# Revit family: Lighting_Pendants_Nordlux_Angle_E27
name_source: partatom
category: Lighting Fixtures
revit_build: Autodesk Revit 2017 (Build: 20190508_0315(x64)
units: mm (PartAtom-declared; Revit-internal decimal feet)

## family parameters
Always vertical = Yes
Cut with Voids When Loaded = No
Light Source = Yes
OmniClass Number = 23.80.70.00
OmniClass Title = Lighting
Part Type = Normal
Room Calculation Point = No
Round Connector Dimension = Use Diameter
Shared = No
Work Plane-Based = No

## types (3) — shared parameters
AssetType = Fixed
BIMObjectName = Lighting_Pendants_Nordlux_Angle_E27
Brand = Nordlux
Category = Pendants
Collection = Angle E27
Color Filter = 16777215
ConvergoRefNr = 0143-2009-0015-DK
DefaultElevation = 4000 mm  [stored 13.1234 ft]
Designer = Maria Berntsen
Dimming Lamp Color Temperature Shift = <None>
DurationUnit = Hours
Features = Lamp can be dimmed with compatible bulb.Magnet on the textile cord for directing the light in any direction.
HasProtectiveEarth = No
IP_Code = IP20
IfcExportAs = IfcLightFixtureType
IfcExportType = NOTDEFINED
InsulationStandardClass = Class 2 Double Isolated
Light Source Symbol Length = 300 mm
LightFixtureMountingType = Suspended
LightFixturePlacingType = Ceiling
Manufacturer = Nordlux
ManufacturerName = Nordlux
ManufacturerURL = https://www.nordlux.com
Material = Metal & Plastic
NBSDescription = General purpose luminaires
NBSReference = 90-60-50/405
Name = Angle_E27
NominalCurrent = 0 A
NominalDiameter = 206 mm
NominalFrequencyRange = 50 Hz
NominalHeight = 247 mm
NominalLength = 206 mm
NominalRadius = 103 mm
NominalVoltage = 230 V
NominalVoltageCalc = 0 V
NominalWidth = 206 mm
NumberOfPoles = 1
PhaseAngle = 0.00°
ProductDatasheet = http://pim.skypim.com
Shape = Sculptured
Size = 206x206x247 mm
Spot Beam Angle = 30.00°
Spot Field Angle = 90.00°
Tilt Angle = 90.00°
TotalWattage = 60 W
URL = https://www.nordlux.com
Uniclass2 = Pr_70_70_49_86
Uniclass2015Description = Pendant luminaires
Uniclass2015Reference = Pr_70_70_48_62
UsageCurrent = 0 A
Version = 1
VersionDate = 19/11/2020
WarrantyDurationUnit = Hours
zero-valued in all types: Cost, ElectricalDeviceNominalPower, MaintenanceFactor, NumberOfSources

## per-type parameters (varying)
| type | ArticleNumber | Color | Description | EAN Number | LightFixtureMainMaterial | LightFixtureSecondaryMaterial | ModelReference | ProductInformation |
| Angle E27 - Black | 2020673003 | Black | Angle is contemporary and exclusive lighting with an industrial look. The special feature of this lamp is the ability to determine the direction of the light via the magnet mounted on the cord. The lamp looks great in clusters of several units which are angled differently. It creates a gorgeous expression and adds a bit of ambience to any room. Designed by Maria Berntsen. Angle in black is very modern and has lots of uses – for example, use it to illuminate the reading corner or in the kitchen, where the light can be directed to where the need is particularly great. | 5704924003035 | Black Metal | Plastic, Opaque Black | 2020673003 | Angle is contemporary and exclusive lighting with an industrial look. The special feature of this lamp is the ability to determine the direction of the light via the magnet mounted on the cord. The lamp looks great in clusters of several units which are angled differently. It creates a gorgeous expression and adds a bit of ambience to any room. Designed by Maria Berntsen. Angle in black is very modern and has lots of uses – for example, use it to illuminate the reading corner or in the kitchen, where the light can be directed to where the need is particularly great. |
| Angle E27 - White-grey | 2020673001 | White-grey | Angle is contemporary and exclusive lighting with an industrial look. The special feature of this lamp is the ability to determine the direction of the light via the magnet mounted on the cord. The lamp looks great in clusters of several units which are angled differently. It creates a gorgeous expression and adds a bit of ambience to any room. Designed by Maria Berntsen. Angle in white-grey is very modern and has lots of uses – for example, use it to illuminate the reading corner or in the kitchen, where the light can be directed to where the need is particularly great. | 5704924003028 | White Metal | Plastic, Opaque White | 2020673001 | Angle is contemporary and exclusive lighting with an industrial look. The special feature of this lamp is the ability to determine the direction of the light via the magnet mounted on the cord. The lamp looks great in clusters of several units which are angled differently. It creates a gorgeous expression and adds a bit of ambience to any room. Designed by Maria Berntsen. Angle in white-grey is very modern and has lots of uses – for example, use it to illuminate the reading corner or in the kitchen, where the light can be directed to where the need is particularly great. |
| Angle E27 - Grey | 2020673011 | Grey | Angle is contemporary and exclusive lighting with an industrial look. The special feature of this lamp is the ability to determine the direction of the light via the magnet mounted on the cord. The lamp looks great in clusters of several units which are angled differently. It creates a gorgeous expression and adds a bit of ambience to any room. Designed by Maria Berntsen. Angle in grey is very modern and has lots of uses – for example, use it to illuminate the reading corner or in the kitchen, where the light can be directed to where the need is particularly great. | 5704924003042 | Grey Metal | Plastic, Opaque Grey | 2020673011 | Angle is contemporary and exclusive lighting with an industrial look. The special feature of this lamp is the ability to determine the direction of the light via the magnet mounted on the cord. The lamp looks great in clusters of several units which are angled differently. It creates a gorgeous expression and adds a bit of ambience to any room. Designed by Maria Berntsen. Angle in grey is very modern and has lots of uses – for example, use it to illuminate the reading corner or in the kitchen, where the light can be directed to where the need is particularly great. |

note: column(s) folded — value = type name in every type: Model

note: [stored X ft] marks values corroborated as IEEE doubles in the binary element streams (Revit-internal decimal feet)

## geometry (parser evidence)
native form markers: Sweep x11
no freeform markers — native parametric forms only
